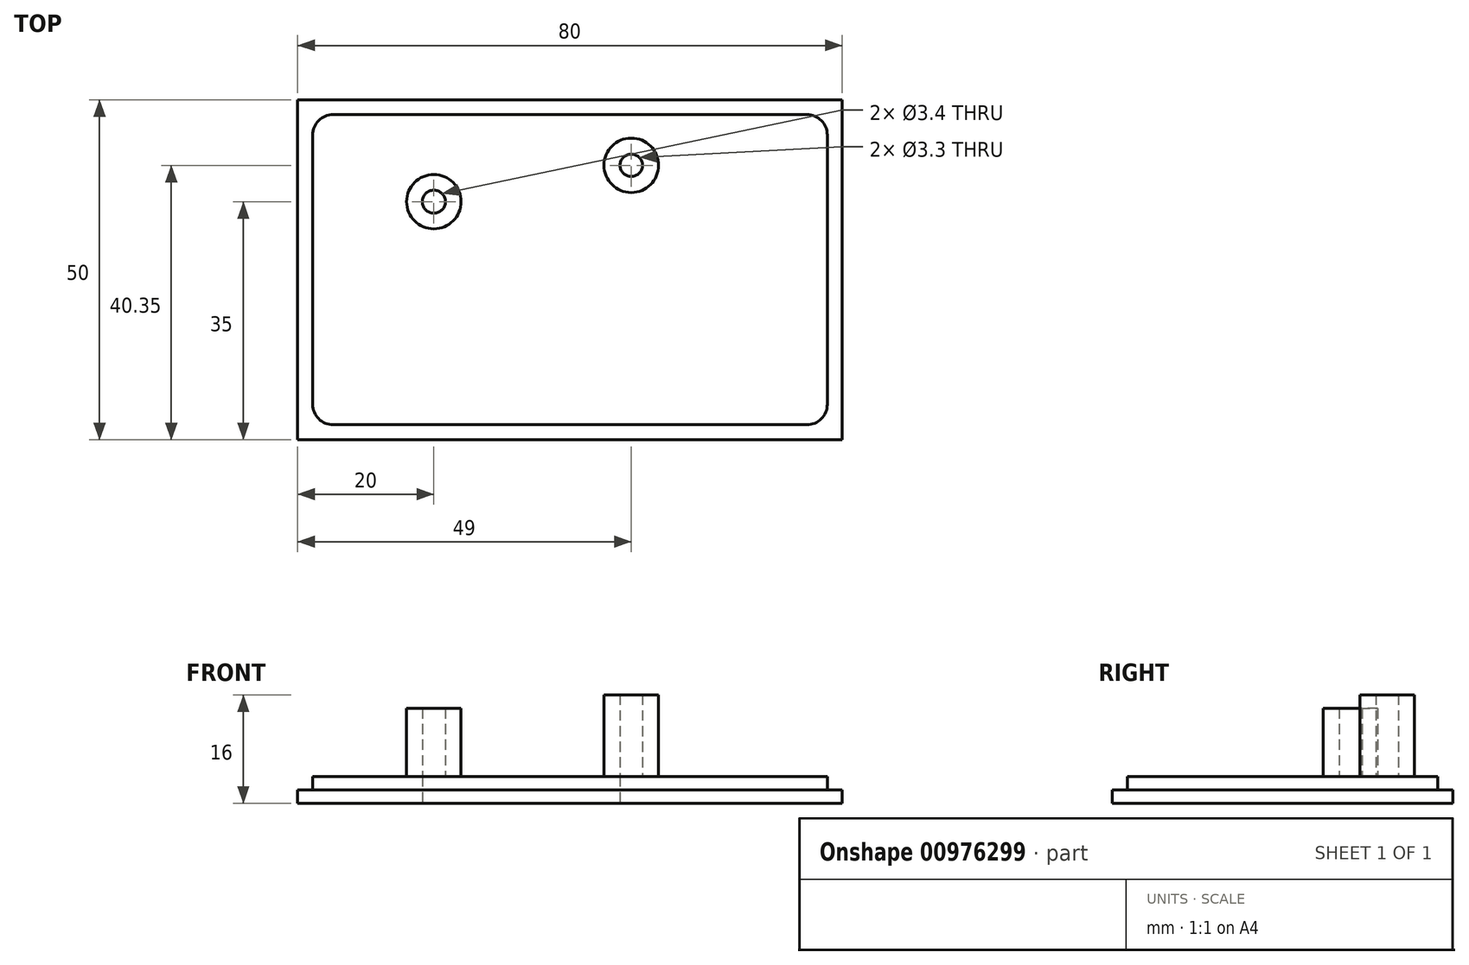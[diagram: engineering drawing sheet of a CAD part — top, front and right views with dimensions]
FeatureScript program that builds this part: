
annotation { "Feature Type Name" : "Feature", "Feature Type Description" : "" }
export const myFeature = defineFeature(function(context is Context, id is Id, definition is map)
    precondition{}
    {
        {
            var Q0;
            Q0=qCreatedBy(makeId("Top.planeOp"),FACE);
            var sketch = newSketch(context, id + "F0", { "sketchPlane" : qUnion([Q0])});
            skLineSegment(sketch, "E0.bottom", {"start": v(40, -25) * mm, "end": v(-40, -25) * mm});
            skLineSegment(sketch, "E0.top", {"start": v(40, 25) * mm, "end": v(-40, 25) * mm});
            skLineSegment(sketch, "E0.left", {"start": v(40, -25) * mm, "end": v(40, 25) * mm});
            skLineSegment(sketch, "E0.right", {"start": v(-40, -25) * mm, "end": v(-40, 25) * mm});
            skPoint(sketch, "E0.middle", {"position": v(0, 0) * mm});
            skSolve(sketch);
        }
        {
            var Q0;
            Q0=makeQuery(id+"F0.imprint","IMPRINT",FACE,{"disambiguationData":[TD([[makeQuery(id+"F0.imprint","IMPRINT",EDGE,{"derivedFrom":sQuery(id+"F0.wireOp",EDGE,"E0.bottom")}),-1.0]])]});
            extrude(context, id + "F1", {"entities" : qUnion([Q0]), "depth" : 2 * mm, "offsetDistance" : 25 * mm});
        }
        {
            var Q0;
            Q0=makeQuery(id+"F1.opExtrude","CAP_FACE",FACE,{"disambiguationData":[OSD([sQuery(id+"F0.wireOp",EDGE,"E0.bottom"),sQuery(id+"F0.wireOp",EDGE,"E0.top"),sQuery(id+"F0.wireOp",EDGE,"E0.left"),sQuery(id+"F0.wireOp",EDGE,"E0.right")])],"isStart":false});
            var sketch = newSketch(context, id + "F2", { "sketchPlane" : qUnion([Q0])});
            skLineSegment(sketch, "E1.bottom", {"start": v(37.8, -22.8) * mm, "end": v(-37.8, -22.8) * mm});
            skLineSegment(sketch, "E1.top", {"start": v(37.8, 22.8) * mm, "end": v(-37.8, 22.8) * mm});
            skLineSegment(sketch, "E1.left", {"start": v(37.8, -22.8) * mm, "end": v(37.8, 22.8) * mm});
            skLineSegment(sketch, "E1.right", {"start": v(-37.8, -22.8) * mm, "end": v(-37.8, 22.8) * mm});
            skPoint(sketch, "E1.middle", {"position": v(0, 0) * mm});
            skSolve(sketch);
        }
        {
            var Q0;
            Q0 = qSketchRegion(id + "F2", true);
            extrude(context, id + "F3", {"entities" : qUnion([Q0]), "operationType" : NewBodyOperationType.ADD, "depth" : 2 * mm, "offsetDistance" : 25 * mm});
        }
        {
            var Q0;
            Q0=makeQuery(id+"F3.opExtrude","SWEPT_EDGE",EDGE,{"disambiguationData":[OSD([sQuery(id+"F2.wireOp",EDGE,"E1.top"),sQuery(id+"F2.wireOp",EDGE,"E1.right")])]});
            var Q1;
            Q1=makeQuery(id+"F3.opExtrude","SWEPT_EDGE",EDGE,{"disambiguationData":[OSD([sQuery(id+"F2.wireOp",EDGE,"E1.bottom"),sQuery(id+"F2.wireOp",EDGE,"E1.right")])]});
            var Q2;
            Q2=makeQuery(id+"F3.opExtrude","SWEPT_EDGE",EDGE,{"disambiguationData":[OSD([sQuery(id+"F2.wireOp",EDGE,"E1.top"),sQuery(id+"F2.wireOp",EDGE,"E1.left")])]});
            var Q3;
            Q3=makeQuery(id+"F3.opExtrude","SWEPT_EDGE",EDGE,{"disambiguationData":[OSD([sQuery(id+"F2.wireOp",EDGE,"E1.bottom"),sQuery(id+"F2.wireOp",EDGE,"E1.left")])]});
            fillet(context, id + "F4", {"entities" : qUnion([Q0, Q1, Q2, Q3]), "radius" : 3 * mm, "tangentPropagation" : true, "allowEdgeOverflow" : false});
        }
        {
            var Q0;
            Q0=makeQuery(id+"F1.opExtrude","CAP_FACE",FACE,{"disambiguationData":[OSD([sQuery(id+"F0.wireOp",EDGE,"E0.bottom"),sQuery(id+"F0.wireOp",EDGE,"E0.top"),sQuery(id+"F0.wireOp",EDGE,"E0.left"),sQuery(id+"F0.wireOp",EDGE,"E0.right")])],"isStart":true});
            var sketch = newSketch(context, id + "F5", { "sketchPlane" : qUnion([Q0])});
            skCircle(sketch, "E2", {"center": v(-20, -10) * mm, "radius": 1.7 * mm});
            skCircle(sketch, "E3", {"center": v(9, -15.35) * mm, "radius": 1.65 * mm});
            skSolve(sketch);
        }
        {
            var Q0;
            Q0=makeQuery(id+"F5.imprint","IMPRINT",FACE,{"disambiguationData":[TD([[makeQuery(id+"F5.imprint","IMPRINT",EDGE,{"derivedFrom":sQuery(id+"F5.wireOp",EDGE,"E2")}),1.0]])]});
            var Q1;
            Q1=makeQuery(id+"F5.imprint","IMPRINT",FACE,{"disambiguationData":[TD([[makeQuery(id+"F5.imprint","IMPRINT",EDGE,{"derivedFrom":sQuery(id+"F5.wireOp",EDGE,"E3")}),1.0]])]});
            extrude(context, id + "F6", {"entities" : qUnion([Q0, Q1]), "operationType" : NewBodyOperationType.REMOVE, "oppositeDirection" : true, "depth" : 25 * mm, "offsetDistance" : 25 * mm});
        }
        {
            var Q0;
            Q0=makeQuery(id+"F3.opExtrude","CAP_FACE",FACE,{"disambiguationData":[OSD([sQuery(id+"F2.wireOp",EDGE,"E1.bottom"),sQuery(id+"F2.wireOp",EDGE,"E1.top"),sQuery(id+"F2.wireOp",EDGE,"E1.left"),sQuery(id+"F2.wireOp",EDGE,"E1.right")])],"isStart":false});
            var sketch = newSketch(context, id + "F7", { "sketchPlane" : qUnion([Q0])});
            skCircle(sketch, "E4", {"center": v(9, 15.35) * mm, "radius": 4 * mm});
            skSolve(sketch);
        }
        {
            var Q0;
            Q0=makeQuery(id+"F7.imprint","IMPRINT",FACE,{"disambiguationData":[TD([[makeQuery(id+"F7.imprint","IMPRINT",EDGE,{"derivedFrom":sQuery(id+"F7.wireOp",EDGE,"E4")}),1.0]])]});
            extrude(context, id + "F8", {"entities" : qUnion([Q0]), "depth" : 12 * mm, "offsetDistance" : 25 * mm});
        }
        {
            var Q0;
            Q0=makeQuery(id+"F3.opExtrude","CAP_FACE",FACE,{"disambiguationData":[OSD([sQuery(id+"F2.wireOp",EDGE,"E1.bottom"),sQuery(id+"F2.wireOp",EDGE,"E1.top"),sQuery(id+"F2.wireOp",EDGE,"E1.left"),sQuery(id+"F2.wireOp",EDGE,"E1.right")])],"isStart":false});
            var sketch = newSketch(context, id + "F9", { "sketchPlane" : qUnion([Q0])});
            skCircle(sketch, "E5", {"center": v(-20, 10) * mm, "radius": 4 * mm});
            skSolve(sketch);
        }
        {
            var Q0;
            Q0=makeQuery(id+"F9.imprint","IMPRINT",FACE,{"disambiguationData":[TD([[makeQuery(id+"F9.imprint","IMPRINT",EDGE,{"derivedFrom":sQuery(id+"F9.wireOp",EDGE,"E5")}),1.0]])]});
            var Q1;
            Q1=sQuery(id+"F9.wireOp",EDGE,"E5");
            extrude(context, id + "F10", {"entities" : qUnion([Q0]), "surfaceEntities" : qUnion([Q1]), "depth" : 10 * mm, "offsetDistance" : 25 * mm});
        }
    });
